# Revit family: RVi-IPC31S (2.8-12 мм)
name_source: partatom
category: Устройства связи
revit_build: Autodesk Revit 2016 (Build: 20161004_0715(x64)
units: mm (PartAtom-declared; Revit-internal decimal feet)

## family parameters
Всегда вертикально = Да
На основе рабочей плоскости = Да
Общий = Нет
При загрузке вырезать с полостями = Нет
Размер круглого соединителя = Использовать диаметр
Сохранять ориентацию аннотаций = Нет
Тип детали = Нормальный
Точка расчета площади = Нет

## types (1)
- Стандартная
    2D.Телекамера в герметичном термокожухе = Нет
    2D.Телекамера с поворотным устройством = Нет
    Bullet.корпус = Без корпуса : Пусто
    Bullet.крепление = Без крепления : Пусто
    Kr_max = 60.00°
    Kr_min = -60.00°
    RVi.Аудио.Вход = Да
    RVi.Аудио.Выход = Да
    RVi.Аудио.Динамик = Нет
    RVi.Аудио.Микрофон = Нет
    RVi.ИК подсветка.Дальность = 30000 мм
    RVi.Карта памяти = Да
    RVi.Питание 12В = Да
    RVi.Питание 24В = Нет
    RVi.Питание POE = Да
    RVi.Разрешение = 1280×720
    RVi.Тип корпуса = Купольные
    RVi.Тип продукта = Камеры внутренней установки
    RVi.Тревога = Да
    RVi.Функция аналитики = Да
    Rn_max = 75.00°
    Rn_min = 0.00°
    Ro_max = 177.50°
    Ro_min = -177.50°
    URL = http://rvi-cctv.ru
    Ug_max = 98.00°
    Ug_min = 30.20°
    Uv_max = 71.00°
    Uv_min = 22.00°
    Вращение всей камеры = 0.00°
    Группа модели = Камера в сборе
    Длина неподвижной части корпуса = 53 мм
    Длина подвижной части = 0 мм
    Изготовитель = RVi
    К идентификации = 250
    К обнаружения = 20
    К распознавания номера = 240
    К распознования = 100
    Крепление = Без крепления : Пусто
    Купол.корпус = Корпус 31S : Тип
    Купол.обектив = Без корпуса : Пусто
    Купольная камера = Да
    Материал корпуса камеры = Камера.корпус
    Материал крепления = Камера.крепление
    Материал объектива камеры = Камера.объектив
    Наименование и техническая характеристика = Купольная IP-камера; 1/3” КМОП, Формат сжатия: H.264/MJPEG; Максимальное разрешение и скорость трансляции: 1280х960  (25 к/с); Нижний порог чувствительности: 0.01 лк @ F1.2 цвет / 0.001 лк @ F1.2 ч.б.; Объектив: 2.8-12  мм; ИК-подсветка: до 30 метров; Аудио вх./вых.: 1/1; Встроенная видеоаналитика; Micro SD; Диапазон рабочих температур: -10…+50°С; Питание: PoE 802.3af / DC 12 В, 5,5 Вт;
    Обектив коррекция наклона = 0.00°
    Отметка по умолчанию = 1219 мм
    Поворот направления взгляда = 0.00°
    Смещение объектива = 50 мм
    Стрела длина = 0 мм
    Стрела коррекция = 0.00°
    Стрела угол подъема = 0.00°
    УГО смещение = 200 мм
    да = Да
    нет = Нет

## geometry (parser evidence)
native form markers: Blend x13
no freeform markers — native parametric forms only
